# Revit family: 07721_DAO-H_2R
name_source: partatom
category: Air Terminals
revit_build: Autodesk Revit MEP 2012 (Build: 20110309_2315(x64)
units: mm (PartAtom-declared; Revit-internal decimal feet)

## types (5) — shared parameters
Conect_Largo = 72"
Description = Difusor Lineal Oculto
Función = Inyección
Largo_Requerido = 72"
Longitud Mín-Máx. = 24" (0.6096 mts)  a 141 3/4" (3.60 mts)
Manufacturer = INNES
Material del Difusor = Aluminio y acero
Model = DAO-H-2R
Nota1 = .
Nota2 = .
Posición de Instalación = Muro/Techo
Tipo de Cuello = Rectangular
Type Comments = Descarga Horizontal con 2 Ranuras
URL = https://www.innes.com.mx
Var1 = 36"
Visible_Texto_1 = No
Visible_Texto_2 = No

## per-type parameters (varying)
| type | Conect_Ancho | Separacion |
| Separación 1" | 5" | 1" |
| Separación 2" | 7" | 2" |
| Separación 1.5" | 6" | 1 1/2" |
| Separación 2.5" | 8" | 2 1/2" |
| Separación 3" | 9" | 3" |

## geometry (parser evidence)
native form markers: Sweep x11
no freeform markers — native parametric forms only
